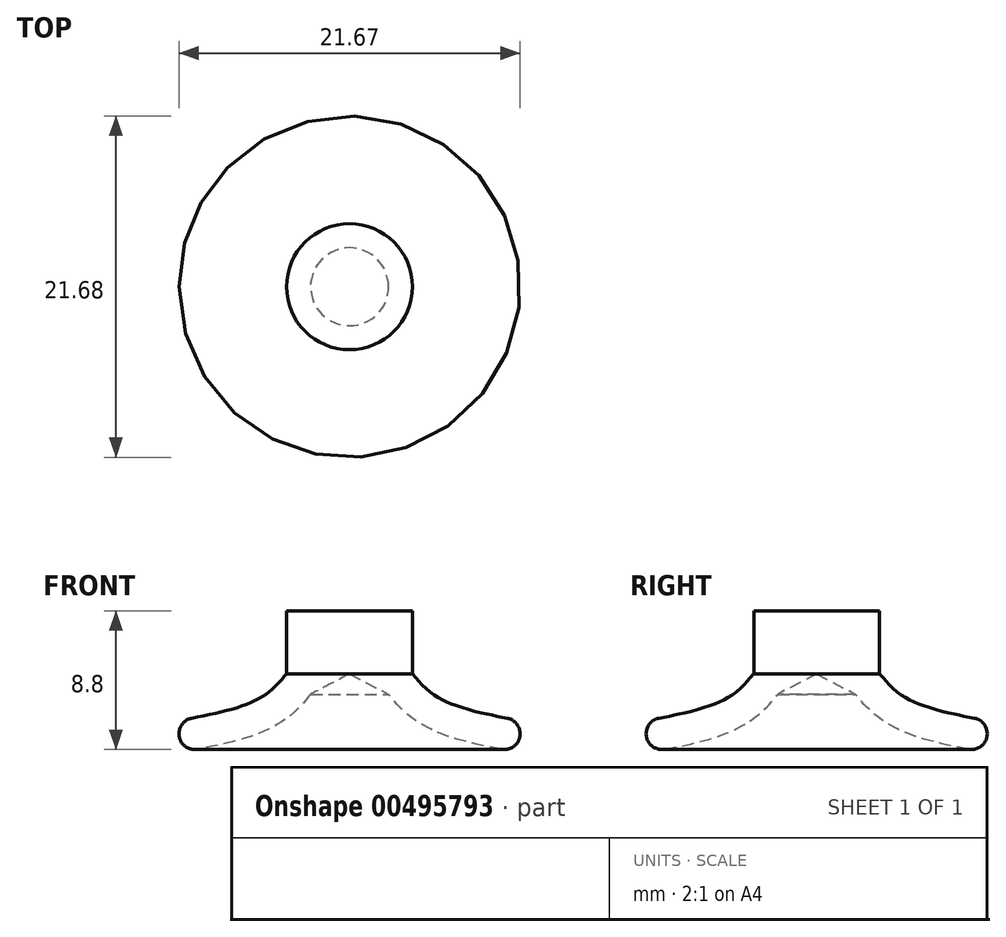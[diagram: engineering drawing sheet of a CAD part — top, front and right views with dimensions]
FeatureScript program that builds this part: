
annotation { "Feature Type Name" : "Feature", "Feature Type Description" : "" }
export const myFeature = defineFeature(function(context is Context, id is Id, definition is map)
    precondition{}
    {
        {
            var Q0;
            Q0=qCreatedBy(makeId("Front.planeOp"),FACE);
            var sketch = newSketch(context, id + "F0", { "sketchPlane" : qUnion([Q0])});
            skLineSegment(sketch, "E0.bottom", {"start": v(-3.1, 3) * mm, "end": v(0.9, 3) * mm});
            skLineSegment(sketch, "E0.top", {"start": v(-3.1, 7) * mm, "end": v(0.9, 7) * mm});
            skLineSegment(sketch, "E0.left", {"start": v(-3.1, 3) * mm, "end": v(-3.1, 7) * mm});
            skLineSegment(sketch, "E0.right", {"start": v(0.9, 3) * mm, "end": v(0.9, 7) * mm});
            skFitSpline(sketch, "E1", {"points": [v(-3.1, 3) * mm, v(-4.9, 1.4) * mm, v(-10.1, 0) * mm], "startDerivative": vector(-3.68, -4.33) * mm, "endDerivative": vector(-9.91, -1.83) * mm});
            skFitSpline(sketch, "E2.0", {"points": [v(-1.57, 1.7) * mm, v(-1.72, 1.52) * mm, v(-2.06, 1.12) * mm, v(-2.64, 0.54) * mm, v(-3.22, 0.08) * mm, v(-3.72, -0.24) * mm, v(-4.27, -0.54) * mm, v(-4.83, -0.78) * mm, v(-5.41, -0.98) * mm, v(-6.2, -1.23) * mm, v(-7.22, -1.48) * mm, v(-8.48, -1.74) * mm, v(-9.31, -1.9) * mm, v(-9.73, -1.97) * mm]});
            skLineSegment(sketch, "E3", {"start": v(-10.1, 0) * mm, "end": v(-9.73, -1.97) * mm});
            skLineSegment(sketch, "E4", {"start": v(-1.57, 1.7) * mm, "end": v(0.9, 3) * mm});
            skSolve(sketch);
        }
        {
            var Q0;
            {var subQ0=sQuery(id+"F0.wireOp",EDGE,"E1");Q0=makeQuery(id+"F0.imprint","IMPRINT",FACE,{"disambiguationData":[TD([[makeQuery(id+"F0.imprint","IMPRINT",EDGE,{"derivedFrom":subQ0}),1.0]])]});}
            var Q1;
            Q1=makeQuery(id+"F0.imprint","IMPRINT",FACE,{"disambiguationData":[TD([[makeQuery(id+"F0.imprint","IMPRINT",EDGE,{"derivedFrom":sQuery(id+"F0.wireOp",EDGE,"E0.top")}),-1.0]])]});
            var Q2;
            Q2=sQuery(id+"F0.wireOp",EDGE,"E0.right");
            revolve(context, id + "F1", {"entities" : qUnion([Q0, Q1]), "axis" : qUnion([Q2]), "revolveType" : RevolveType.FULL});
        }
        {
            var Q0;
            Q0=makeQuery(id+"F1.opRevolve","SWEPT_EDGE",EDGE,{"disambiguationData":[OSD([sQuery(id+"F0.wireOp",EDGE,"E2.0"),sQuery(id+"F0.wireOp",EDGE,"E3")])]});
            var Q1;
            Q1=makeQuery(id+"F1.opRevolve","SWEPT_EDGE",EDGE,{"disambiguationData":[OSD([sQuery(id+"F0.wireOp",EDGE,"E1"),sQuery(id+"F0.wireOp",EDGE,"E3")])]});
            fillet(context, id + "F2", {"entities" : qUnion([Q0, Q1]), "radius" : 1 * mm, "tangentPropagation" : true, "allowEdgeOverflow" : false});
        }
    });
